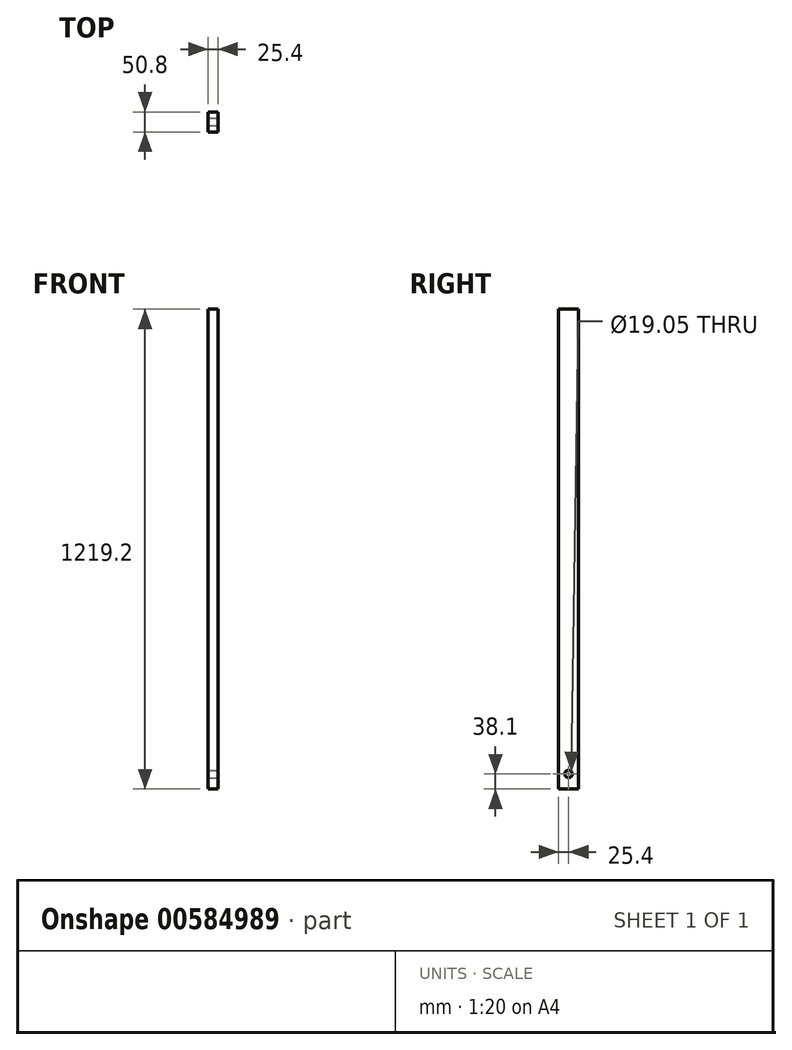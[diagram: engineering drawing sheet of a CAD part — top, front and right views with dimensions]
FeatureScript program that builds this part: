
annotation { "Feature Type Name" : "Feature", "Feature Type Description" : "" }
export const myFeature = defineFeature(function(context is Context, id is Id, definition is map)
    precondition{}
    {
        {
            var Q0;
            Q0=qCreatedBy(makeId("Top.planeOp"),FACE);
            var sketch = newSketch(context, id + "F0", { "sketchPlane" : qUnion([Q0])});
            skLineSegment(sketch, "E0.bottom", {"start": v(13.1, 25.4) * mm, "end": v(-12.3, 25.4) * mm});
            skLineSegment(sketch, "E0.top", {"start": v(13.1, -25.4) * mm, "end": v(-12.3, -25.4) * mm});
            skLineSegment(sketch, "E0.left", {"start": v(13.1, 25.4) * mm, "end": v(13.1, -25.4) * mm});
            skLineSegment(sketch, "E0.right", {"start": v(-12.3, 25.4) * mm, "end": v(-12.3, -25.4) * mm});
            skPoint(sketch, "E0.middle", {"position": v(0.4, 0) * mm});
            skSolve(sketch);
        }
        {
            var Q0;
            Q0=makeQuery(id+"F0.imprint","IMPRINT",FACE,{"disambiguationData":[TD([[makeQuery(id+"F0.imprint","IMPRINT",EDGE,{"derivedFrom":sQuery(id+"F0.wireOp",EDGE,"E0.bottom")}),1.0]])]});
            extrude(context, id + "F1", {"entities" : qUnion([Q0]), "depth" : 1219.2 * mm, "offsetDistance" : 25.4 * mm});
        }
        {
            var Q0;
            Q0=makeQuery(id+"F1.opExtrude","SWEPT_FACE",FACE,{"disambiguationData":[OSD([sQuery(id+"F0.wireOp",EDGE,"E0.left")])]});
            var sketch = newSketch(context, id + "F2", { "sketchPlane" : qUnion([Q0])});
            skPoint(sketch, "E1", {"position": v(0, 38.1) * mm});
            skSolve(sketch);
        }
        {
            var Q0;
            Q0=sQuery(id+"F2.wireOp",VERTEX,"cbd7e0f3-1140-4789-8ecb-e8ac43c8e15e");
            var Q1;
            Q1=sQuery(id+"F2.wireOp",VERTEX,"E1");
            var Q2;
            Q2=makeQuery(id+"F1.opExtrude","SWEPT_BODY",BODY,{"disambiguationData":[OSD([sQuery(id+"F0.wireOp",EDGE,"E0.bottom"),sQuery(id+"F0.wireOp",EDGE,"E0.top"),sQuery(id+"F0.wireOp",EDGE,"E0.left"),sQuery(id+"F0.wireOp",EDGE,"E0.right")])]});
            hole(context, id + "F3", {"style" : HoleStyle.SIMPLE, "endStyle" : HoleEndStyle.THROUGH, "holeDiameter" : 19.05 * mm, "majorDiameter" : 6.35 * mm, "isTappedThrough" : true, "tappedDepth" : 12.7 * mm, "tapClearance" : 3, "locations" : qUnion([Q0, Q1]), "scope" : qUnion([Q2])});
        }
    });
